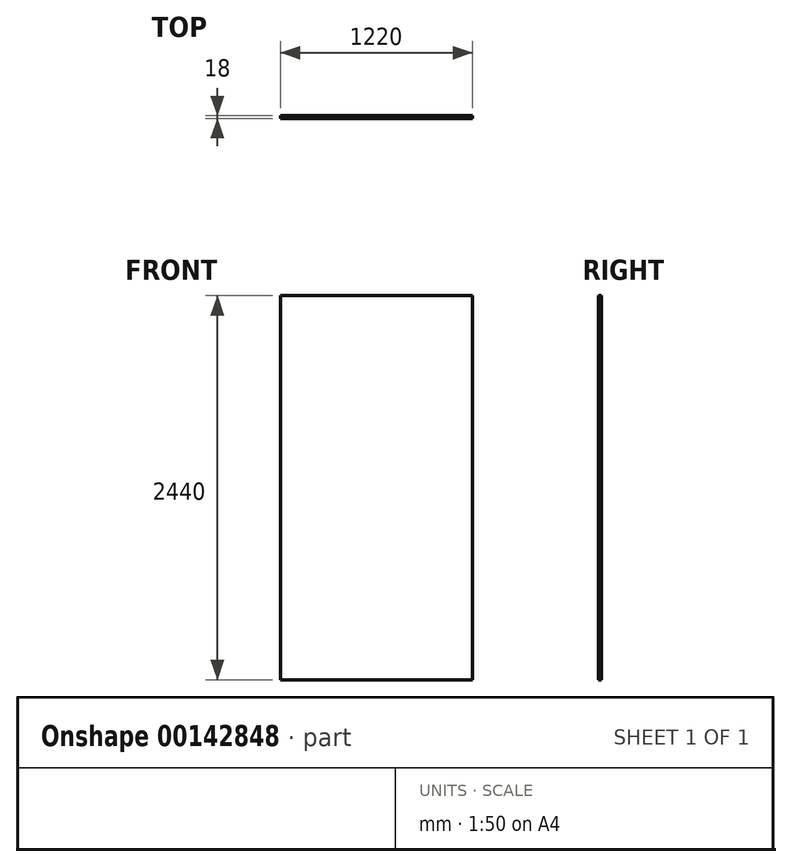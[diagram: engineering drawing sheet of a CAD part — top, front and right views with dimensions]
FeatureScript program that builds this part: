
annotation { "Feature Type Name" : "Feature", "Feature Type Description" : "" }
export const myFeature = defineFeature(function(context is Context, id is Id, definition is map)
    precondition{}
    {
        {
            var Q0;
            Q0=qCreatedBy(makeId("Front.planeOp"),FACE);
            var sketch = newSketch(context, id + "F0", { "sketchPlane" : qUnion([Q0])});
            skLineSegment(sketch, "E0.bottom", {"start": v(0, 0) * mm, "end": v(1220, 0) * mm});
            skLineSegment(sketch, "E0.top", {"start": v(0, 2440) * mm, "end": v(1220, 2440) * mm});
            skLineSegment(sketch, "E0.left", {"start": v(0, 0) * mm, "end": v(0, 2440) * mm});
            skLineSegment(sketch, "E0.right", {"start": v(1220, 0) * mm, "end": v(1220, 2440) * mm});
            skSolve(sketch);
        }
        {
            var Q0;
            Q0 = qSketchRegion(id + "F0", true);
            extrude(context, id + "F1", {"entities" : qUnion([Q0]), "depth" : 18 * mm});
        }
    });
